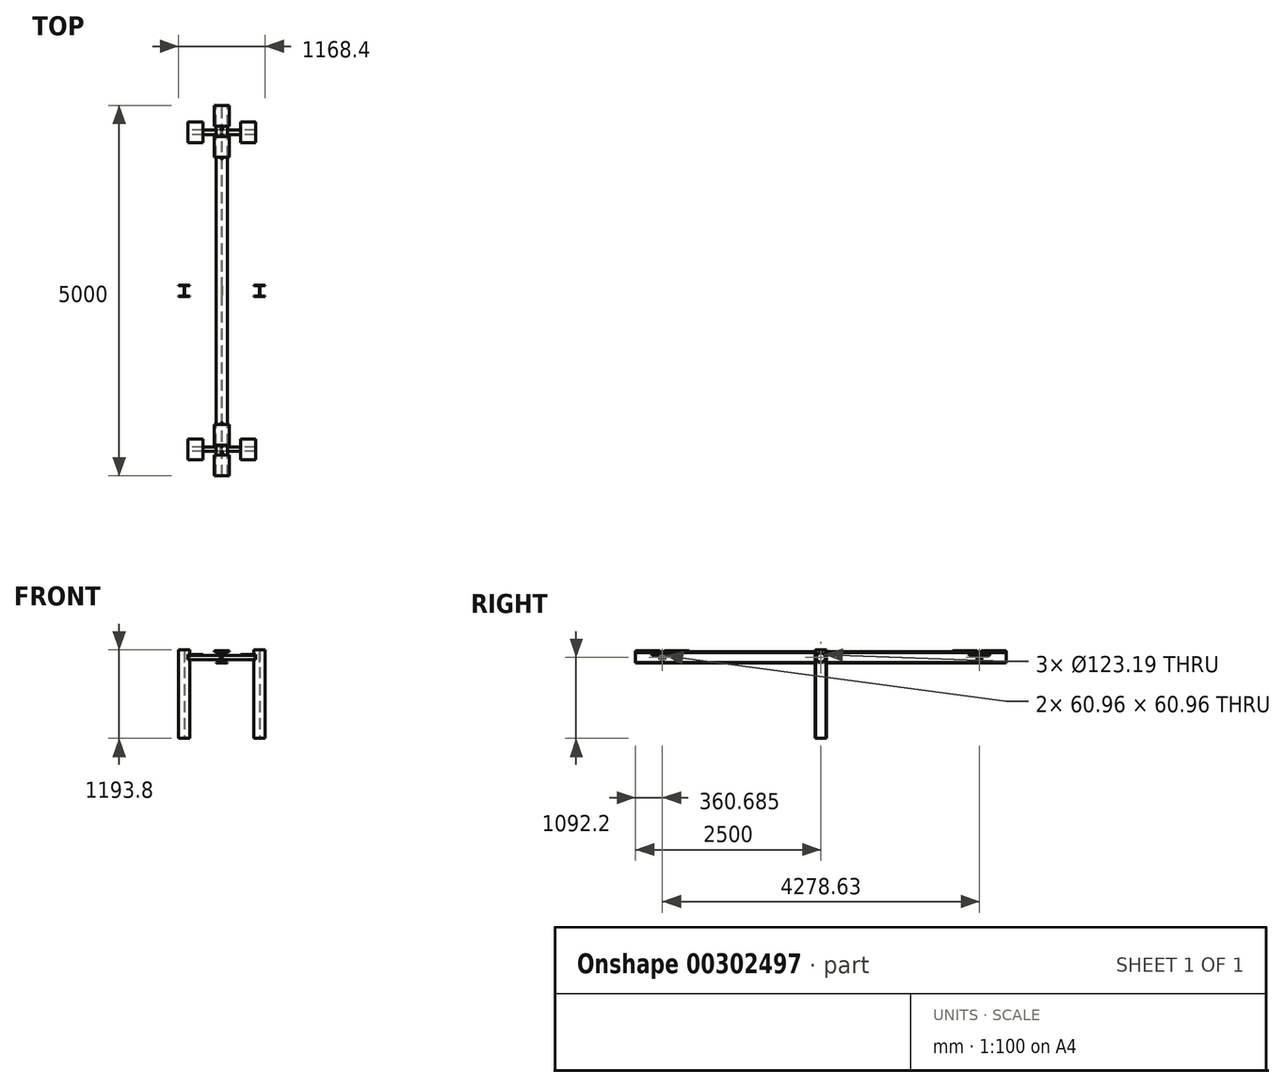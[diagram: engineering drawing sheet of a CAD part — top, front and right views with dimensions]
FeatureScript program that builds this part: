
annotation { "Feature Type Name" : "Feature", "Feature Type Description" : "" }
export const myFeature = defineFeature(function(context is Context, id is Id, definition is map)
    precondition{}
    {
        {
            var Q0;
            Q0=qCreatedBy(makeId("Right.planeOp"),FACE);
            var sketch = newSketch(context, id + "F0", { "sketchPlane" : qUnion([Q0])});
            skCircle(sketch, "E0", {"center": v(0, 0) * mm, "radius": 60.96 * mm});
            skSolve(sketch);
        }
        {
            var Q0;
            Q0 = qSketchRegion(id + "F0", true);
            extrude(context, id + "F1", {"entities" : qUnion([Q0]), "endBound" : BoundingType.SYMMETRIC, "depth" : 1092.2 * mm});
        }
        {
            var Q0;
            Q0=qCreatedBy(makeId("Front.planeOp"),FACE);
            var sketch = newSketch(context, id + "F2", { "sketchPlane" : qUnion([Q0])});
            skLineSegment(sketch, "E1.bottom", {"start": v(-76.2, 76.2) * mm, "end": v(76.2, 76.2) * mm});
            skLineSegment(sketch, "E1.top", {"start": v(-76.2, -76.2) * mm, "end": v(76.2, -76.2) * mm});
            skPoint(sketch, "E1.middle", {"position": v(0, 0) * mm});
            skLineSegment(sketch, "E2", {"start": v(-76.2, 76.2) * mm, "end": v(-76.2, 69.09) * mm});
            skLineSegment(sketch, "E3", {"start": v(-76.2, 69.09) * mm, "end": v(-3.05, 69.09) * mm});
            skLineSegment(sketch, "E4", {"start": v(-3.05, 69.09) * mm, "end": v(-3.05, -69.09) * mm});
            skLineSegment(sketch, "E5", {"start": v(-3.05, -69.09) * mm, "end": v(-76.2, -69.09) * mm});
            skLineSegment(sketch, "E6", {"start": v(-76.2, -69.09) * mm, "end": v(-76.2, -76.2) * mm});
            skLineSegment(sketch, "E7", {"start": v(76.2, -76.2) * mm, "end": v(76.2, -69.09) * mm});
            skLineSegment(sketch, "E8", {"start": v(76.2, -69.09) * mm, "end": v(3.05, -69.09) * mm});
            skLineSegment(sketch, "E9", {"start": v(3.05, -69.09) * mm, "end": v(3.05, 69.09) * mm});
            skLineSegment(sketch, "E10", {"start": v(3.05, 69.09) * mm, "end": v(76.2, 69.09) * mm});
            skLineSegment(sketch, "E11", {"start": v(76.2, 69.09) * mm, "end": v(76.2, 76.2) * mm});
            skLineSegment(sketch, "E12", {"start": v(0, 0) * mm, "end": v(507.97, -5.28) * mm, "construction": true});
            skSolve(sketch);
        }
        {
            var Q0;
            Q0 = qSketchRegion(id + "F2", true);
            extrude(context, id + "F3", {"entities" : qUnion([Q0]), "endBound" : BoundingType.SYMMETRIC, "depth" : 4999.99 * mm});
        }
        {
            var Q0;
            Q0=qCreatedBy(makeId("Top.planeOp"),FACE);
            var sketch = newSketch(context, id + "F4", { "sketchPlane" : qUnion([Q0])});
            skLineSegment(sketch, "E13", {"start": v(0, 0) * mm, "end": v(508, 0) * mm});
            skLineSegment(sketch, "E14.bottom", {"start": v(431.8, 76.2) * mm, "end": v(584.2, 76.2) * mm});
            skLineSegment(sketch, "E14.top", {"start": v(431.8, -76.2) * mm, "end": v(584.2, -76.2) * mm});
            skPoint(sketch, "E14.middle", {"position": v(508, 0) * mm});
            skLineSegment(sketch, "E15", {"start": v(431.8, 76.2) * mm, "end": v(431.8, 69.09) * mm});
            skLineSegment(sketch, "E16", {"start": v(431.8, 69.09) * mm, "end": v(504.95, 69.09) * mm});
            skLineSegment(sketch, "E17", {"start": v(504.95, 69.09) * mm, "end": v(504.95, -69.09) * mm});
            skLineSegment(sketch, "E18", {"start": v(504.95, -69.09) * mm, "end": v(431.8, -69.09) * mm});
            skLineSegment(sketch, "E19", {"start": v(431.8, -69.09) * mm, "end": v(431.8, -76.2) * mm});
            skLineSegment(sketch, "E20", {"start": v(584.2, -76.2) * mm, "end": v(584.2, -69.09) * mm});
            skLineSegment(sketch, "E21", {"start": v(584.2, -69.09) * mm, "end": v(511.05, -69.09) * mm});
            skLineSegment(sketch, "E22", {"start": v(511.05, -69.09) * mm, "end": v(511.05, 69.09) * mm});
            skLineSegment(sketch, "E23", {"start": v(511.05, 69.09) * mm, "end": v(584.2, 69.09) * mm});
            skLineSegment(sketch, "E24", {"start": v(584.2, 69.09) * mm, "end": v(584.2, 76.2) * mm});
            skLineSegment(sketch, "E25.MirrorCS", {"start": v(-431.8, 69.09) * mm, "end": v(-504.95, 69.09) * mm});
            skLineSegment(sketch, "E26.MirrorCS", {"start": v(-431.8, 76.2) * mm, "end": v(-584.2, 76.2) * mm});
            skLineSegment(sketch, "E27.MirrorCS", {"start": v(-431.8, 76.2) * mm, "end": v(-431.8, 69.09) * mm});
            skLineSegment(sketch, "E28.MirrorCS", {"start": v(-584.2, -76.2) * mm, "end": v(-584.2, -69.09) * mm});
            skLineSegment(sketch, "E29.MirrorCS", {"start": v(-431.8, -69.09) * mm, "end": v(-431.8, -76.2) * mm});
            skLineSegment(sketch, "E30.MirrorCS", {"start": v(-431.8, -76.2) * mm, "end": v(-584.2, -76.2) * mm});
            skLineSegment(sketch, "E31.MirrorCS", {"start": v(-504.95, 69.09) * mm, "end": v(-504.95, -69.09) * mm});
            skLineSegment(sketch, "E32.MirrorCS", {"start": v(-504.95, -69.09) * mm, "end": v(-431.8, -69.09) * mm});
            skPoint(sketch, "E33.MirrorP", {"position": v(-508, 0) * mm});
            skLineSegment(sketch, "E34.MirrorCS", {"start": v(-511.05, -69.09) * mm, "end": v(-511.05, 69.09) * mm});
            skLineSegment(sketch, "E35.MirrorCS", {"start": v(-584.2, -69.09) * mm, "end": v(-511.05, -69.09) * mm});
            skLineSegment(sketch, "E36.MirrorCS", {"start": v(-511.05, 69.09) * mm, "end": v(-584.2, 69.09) * mm});
            skLineSegment(sketch, "E37.MirrorCS", {"start": v(0, 0) * mm, "end": v(-508, 0) * mm});
            skLineSegment(sketch, "E38.MirrorCS", {"start": v(-584.2, 69.09) * mm, "end": v(-584.2, 76.2) * mm});
            skSolve(sketch);
        }
        {
            var Q0;
            Q0 = qSketchRegion(id + "F4", true);
            extrude(context, id + "F5", {"entities" : qUnion([Q0]), "oppositeDirection" : true, "depth" : 1092.2 * mm});
        }
        {
            var Q0;
            Q0=makeQuery(id+"F5.opExtrude","CAP_FACE",FACE,{"disambiguationData":[OSD([sQuery(id+"F4.wireOp",EDGE,"E27.MirrorCS"),sQuery(id+"F4.wireOp",EDGE,"E29.MirrorCS"),sQuery(id+"F4.wireOp",EDGE,"E38.MirrorCS"),sQuery(id+"F4.wireOp",EDGE,"E28.MirrorCS"),sQuery(id+"F4.wireOp",EDGE,"E26.MirrorCS"),sQuery(id+"F4.wireOp",EDGE,"E30.MirrorCS"),sQuery(id+"F4.wireOp",EDGE,"E25.MirrorCS"),sQuery(id+"F4.wireOp",EDGE,"E31.MirrorCS"),sQuery(id+"F4.wireOp",EDGE,"E36.MirrorCS"),sQuery(id+"F4.wireOp",EDGE,"E35.MirrorCS"),sQuery(id+"F4.wireOp",EDGE,"E32.MirrorCS"),sQuery(id+"F4.wireOp",EDGE,"E34.MirrorCS")])],"isStart":true});
            var Q1;
            Q1=makeQuery(id+"F5.opExtrude","CAP_FACE",FACE,{"disambiguationData":[OSD([sQuery(id+"F4.wireOp",EDGE,"E14.bottom"),sQuery(id+"F4.wireOp",EDGE,"E14.top"),sQuery(id+"F4.wireOp",EDGE,"E15"),sQuery(id+"F4.wireOp",EDGE,"E16"),sQuery(id+"F4.wireOp",EDGE,"E17"),sQuery(id+"F4.wireOp",EDGE,"E18"),sQuery(id+"F4.wireOp",EDGE,"E19"),sQuery(id+"F4.wireOp",EDGE,"E20"),sQuery(id+"F4.wireOp",EDGE,"E21"),sQuery(id+"F4.wireOp",EDGE,"E22"),sQuery(id+"F4.wireOp",EDGE,"E23"),sQuery(id+"F4.wireOp",EDGE,"E24")])],"isStart":true});
            extrude(context, id + "F6", {"entities" : qUnion([Q0, Q1]), "depth" : 101.6 * mm});
        }
        {
            var Q0;
            Q0=makeQuery(id+"F6.opExtrude","SWEPT_BODY",BODY,{"disambiguationData":[OSD([sQuery(id+"F4.wireOp",EDGE,"E27.MirrorCS"),sQuery(id+"F4.wireOp",EDGE,"E29.MirrorCS"),sQuery(id+"F4.wireOp",EDGE,"E38.MirrorCS"),sQuery(id+"F4.wireOp",EDGE,"E28.MirrorCS"),sQuery(id+"F4.wireOp",EDGE,"E26.MirrorCS"),sQuery(id+"F4.wireOp",EDGE,"E30.MirrorCS"),sQuery(id+"F4.wireOp",EDGE,"E25.MirrorCS"),sQuery(id+"F4.wireOp",EDGE,"E31.MirrorCS"),sQuery(id+"F4.wireOp",EDGE,"E36.MirrorCS"),sQuery(id+"F4.wireOp",EDGE,"E35.MirrorCS"),sQuery(id+"F4.wireOp",EDGE,"E32.MirrorCS"),sQuery(id+"F4.wireOp",EDGE,"E34.MirrorCS")])]});
            var Q1;
            Q1=makeQuery(id+"F5.opExtrude","SWEPT_BODY",BODY,{"disambiguationData":[OSD([sQuery(id+"F4.wireOp",EDGE,"E27.MirrorCS"),sQuery(id+"F4.wireOp",EDGE,"E29.MirrorCS"),sQuery(id+"F4.wireOp",EDGE,"E38.MirrorCS"),sQuery(id+"F4.wireOp",EDGE,"E28.MirrorCS"),sQuery(id+"F4.wireOp",EDGE,"E26.MirrorCS"),sQuery(id+"F4.wireOp",EDGE,"E30.MirrorCS"),sQuery(id+"F4.wireOp",EDGE,"E25.MirrorCS"),sQuery(id+"F4.wireOp",EDGE,"E31.MirrorCS"),sQuery(id+"F4.wireOp",EDGE,"E36.MirrorCS"),sQuery(id+"F4.wireOp",EDGE,"E35.MirrorCS"),sQuery(id+"F4.wireOp",EDGE,"E32.MirrorCS"),sQuery(id+"F4.wireOp",EDGE,"E34.MirrorCS")])]});
            booleanBodies(context, id + "F7", {"operationType" : BooleanOperationType.UNION, "tools" : qUnion([Q0, Q1])});
        }
        {
            var Q0;
            Q0=makeQuery(id+"F6.opExtrude","SWEPT_BODY",BODY,{"disambiguationData":[OSD([sQuery(id+"F4.wireOp",EDGE,"E14.bottom"),sQuery(id+"F4.wireOp",EDGE,"E14.top"),sQuery(id+"F4.wireOp",EDGE,"E15"),sQuery(id+"F4.wireOp",EDGE,"E16"),sQuery(id+"F4.wireOp",EDGE,"E17"),sQuery(id+"F4.wireOp",EDGE,"E18"),sQuery(id+"F4.wireOp",EDGE,"E19"),sQuery(id+"F4.wireOp",EDGE,"E20"),sQuery(id+"F4.wireOp",EDGE,"E21"),sQuery(id+"F4.wireOp",EDGE,"E22"),sQuery(id+"F4.wireOp",EDGE,"E23"),sQuery(id+"F4.wireOp",EDGE,"E24")])]});
            var Q1;
            Q1=makeQuery(id+"F5.opExtrude","SWEPT_BODY",BODY,{"disambiguationData":[OSD([sQuery(id+"F4.wireOp",EDGE,"E14.bottom"),sQuery(id+"F4.wireOp",EDGE,"E14.top"),sQuery(id+"F4.wireOp",EDGE,"E15"),sQuery(id+"F4.wireOp",EDGE,"E16"),sQuery(id+"F4.wireOp",EDGE,"E17"),sQuery(id+"F4.wireOp",EDGE,"E18"),sQuery(id+"F4.wireOp",EDGE,"E19"),sQuery(id+"F4.wireOp",EDGE,"E20"),sQuery(id+"F4.wireOp",EDGE,"E21"),sQuery(id+"F4.wireOp",EDGE,"E22"),sQuery(id+"F4.wireOp",EDGE,"E23"),sQuery(id+"F4.wireOp",EDGE,"E24")])]});
            booleanBodies(context, id + "F8", {"operationType" : BooleanOperationType.UNION, "tools" : qUnion([Q0, Q1])});
        }
        {
            var Q0;
            Q0=makeQuery(id+"F3.opExtrude","SWEPT_FACE",FACE,{"disambiguationData":[OSD([sQuery(id+"F2.wireOp",EDGE,"E9")])]});
            var sketch = newSketch(context, id + "F9", { "sketchPlane" : qUnion([Q0])});
            skCircle(sketch, "E39", {"center": v(0, 0) * mm, "radius": 61.6 * mm});
            skSolve(sketch);
        }
        {
            var Q0;
            Q0 = qSketchRegion(id + "F9", true);
            extrude(context, id + "F10", {"entities" : qUnion([Q0]), "operationType" : NewBodyOperationType.REMOVE, "endBound" : BoundingType.THROUGH_ALL, "oppositeDirection" : true, "depth" : 25.4 * mm});
        }
        {
            var Q0;
            {var subQ0=sQuery(id+"F4.wireOp",EDGE,"E22");Q0=makeQuery(id+"F8.opBoolean","MERGE",FACE,{"derivedFrom":[makeQuery(id+"F5.opExtrude","SWEPT_FACE",FACE,{"disambiguationData":[OSD([subQ0])]}),makeQuery(id+"F6.opExtrude","SWEPT_FACE",FACE,{"disambiguationData":[OSD([subQ0])]})]});}
            var sketch = newSketch(context, id + "F11", { "sketchPlane" : qUnion([Q0])});
            skCircle(sketch, "E40", {"center": v(0, 0) * mm, "radius": 61.6 * mm});
            skSolve(sketch);
        }
        {
            var Q0;
            Q0 = qSketchRegion(id + "F11", true);
            extrude(context, id + "F12", {"entities" : qUnion([Q0]), "operationType" : NewBodyOperationType.REMOVE, "endBound" : BoundingType.THROUGH_ALL, "oppositeDirection" : true, "depth" : 25.4 * mm});
        }
        {
            var Q0;
            {var subQ0=sQuery(id+"F4.wireOp",EDGE,"E34.MirrorCS");Q0=makeQuery(id+"F7.opBoolean","MERGE",FACE,{"derivedFrom":[makeQuery(id+"F5.opExtrude","SWEPT_FACE",FACE,{"disambiguationData":[OSD([subQ0])]}),makeQuery(id+"F6.opExtrude","SWEPT_FACE",FACE,{"disambiguationData":[OSD([subQ0])]})]});}
            var sketch = newSketch(context, id + "F13", { "sketchPlane" : qUnion([Q0])});
            skCircle(sketch, "E41", {"center": v(0, 0) * mm, "radius": 61.6 * mm});
            skSolve(sketch);
        }
        {
            var Q0;
            Q0 = qSketchRegion(id + "F13", true);
            extrude(context, id + "F14", {"entities" : qUnion([Q0]), "operationType" : NewBodyOperationType.REMOVE, "endBound" : BoundingType.THROUGH_ALL, "oppositeDirection" : true, "depth" : 25.4 * mm});
        }
        {
            var Q0;
            Q0=makeQuery(id+"F3.opExtrude","SWEPT_FACE",FACE,{"disambiguationData":[OSD([sQuery(id+"F2.wireOp",EDGE,"E1.bottom")])]});
            var sketch = newSketch(context, id + "F15", { "sketchPlane" : qUnion([Q0])});
            skLineSegment(sketch, "E42", {"start": v(0, 0) * mm, "end": v(0, -2360.3) * mm});
            skLineSegment(sketch, "E43.bottom", {"start": v(-101.6, -2220.6) * mm, "end": v(101.6, -2220.6) * mm});
            skLineSegment(sketch, "E43.top", {"start": v(-101.6, -2500) * mm, "end": v(101.6, -2500) * mm});
            skLineSegment(sketch, "E43.left", {"start": v(-101.6, -2220.6) * mm, "end": v(-101.6, -2500) * mm});
            skLineSegment(sketch, "E43.right", {"start": v(101.6, -2220.6) * mm, "end": v(101.6, -2500) * mm});
            skPoint(sketch, "E43.middle", {"position": v(0, -2360.3) * mm});
            skLineSegment(sketch, "E44.bottom", {"start": v(-101.6, -1804.04) * mm, "end": v(101.6, -1804.04) * mm});
            skLineSegment(sketch, "E44.top", {"start": v(-101.6, -2083.43) * mm, "end": v(101.6, -2083.43) * mm});
            skLineSegment(sketch, "E44.left", {"start": v(-101.6, -1804.04) * mm, "end": v(-101.6, -2083.43) * mm});
            skLineSegment(sketch, "E44.right", {"start": v(101.6, -1804.04) * mm, "end": v(101.6, -2083.43) * mm});
            skPoint(sketch, "E44.middle", {"position": v(0, -1943.74) * mm});
            skCircle(sketch, "E45", {"center": v(0, -2207.9) * mm, "radius": 12.7 * mm});
            skCircle(sketch, "E46", {"center": v(0, -2182.5) * mm, "radius": 12.7 * mm});
            skCircle(sketch, "E47", {"center": v(0, -1791.34) * mm, "radius": 12.7 * mm});
            skCircle(sketch, "E48", {"center": v(0, -2096.14) * mm, "radius": 12.7 * mm});
            skCircle(sketch, "E49.MirrorC", {"center": v(0, 2182.5) * mm, "radius": 12.7 * mm});
            skLineSegment(sketch, "E50.MirrorCS", {"start": v(101.6, 1804.04) * mm, "end": v(101.6, 2083.43) * mm});
            skLineSegment(sketch, "E51.MirrorCS", {"start": v(-101.6, 2220.6) * mm, "end": v(101.6, 2220.6) * mm});
            skLineSegment(sketch, "E52.MirrorCS", {"start": v(-101.6, 2083.43) * mm, "end": v(101.6, 2083.43) * mm});
            skPoint(sketch, "E53.MirrorP", {"position": v(0, 1943.74) * mm});
            skLineSegment(sketch, "E54.MirrorCS", {"start": v(101.6, 2220.6) * mm, "end": v(101.6, 2500) * mm});
            skLineSegment(sketch, "E55.MirrorCS", {"start": v(-101.6, 1804.04) * mm, "end": v(101.6, 1804.04) * mm});
            skCircle(sketch, "E56.MirrorC", {"center": v(0, 2207.9) * mm, "radius": 12.7 * mm});
            skCircle(sketch, "E57.MirrorC", {"center": v(0, 1791.34) * mm, "radius": 12.7 * mm});
            skLineSegment(sketch, "E58.MirrorCS", {"start": v(0, 0) * mm, "end": v(0, 2360.3) * mm});
            skLineSegment(sketch, "E59.MirrorCS", {"start": v(-101.6, 1804.04) * mm, "end": v(-101.6, 2083.43) * mm});
            skCircle(sketch, "E60.MirrorC", {"center": v(0, 2096.14) * mm, "radius": 12.7 * mm});
            skLineSegment(sketch, "E61.MirrorCS", {"start": v(-101.6, 2500) * mm, "end": v(101.6, 2500) * mm});
            skLineSegment(sketch, "E62.MirrorCS", {"start": v(-101.6, 2220.6) * mm, "end": v(-101.6, 2500) * mm});
            skPoint(sketch, "E63.MirrorP", {"position": v(0, 2360.3) * mm});
            skSolve(sketch);
        }
        {
            var Q0;
            Q0 = qSketchRegion(id + "F15", true);
            extrude(context, id + "F16", {"entities" : qUnion([Q0]), "depth" : 12.7 * mm});
        }
        {
            var Q0;
            Q0=qCreatedBy(makeId("Right.planeOp"),FACE);
            var sketch = newSketch(context, id + "F17", { "sketchPlane" : qUnion([Q0])});
            skLineSegment(sketch, "E64", {"start": v(0, 0) * mm, "end": v(-2139.32, 0) * mm});
            skLineSegment(sketch, "E65.bottom", {"start": v(-2169.8, 30.48) * mm, "end": v(-2108.83, 30.48) * mm});
            skLineSegment(sketch, "E65.top", {"start": v(-2169.8, -30.48) * mm, "end": v(-2108.83, -30.48) * mm});
            skLineSegment(sketch, "E65.left", {"start": v(-2169.8, 30.48) * mm, "end": v(-2169.8, -30.48) * mm});
            skLineSegment(sketch, "E65.right", {"start": v(-2108.83, 30.48) * mm, "end": v(-2108.83, -30.48) * mm});
            skPoint(sketch, "E65.middle", {"position": v(-2139.32, 0) * mm});
            skPoint(sketch, "E66.MirrorP", {"position": v(2139.32, 0) * mm});
            skLineSegment(sketch, "E67.MirrorCS", {"start": v(2169.8, -30.48) * mm, "end": v(2108.83, -30.48) * mm});
            skLineSegment(sketch, "E68.MirrorCS", {"start": v(2108.83, 30.48) * mm, "end": v(2108.83, -30.48) * mm});
            skLineSegment(sketch, "E69.MirrorCS", {"start": v(2169.8, 30.48) * mm, "end": v(2108.83, 30.48) * mm});
            skLineSegment(sketch, "E70.MirrorCS", {"start": v(2169.8, 30.48) * mm, "end": v(2169.8, -30.48) * mm});
            skSolve(sketch);
        }
        {
            var Q0;
            Q0 = qSketchRegion(id + "F17", true);
            extrude(context, id + "F18", {"entities" : qUnion([Q0]), "endBound" : BoundingType.SYMMETRIC, "depth" : 914.4 * mm});
        }
        {
            var Q0;
            Q0=makeQuery(id+"F18.opExtrude","SWEPT_FACE",FACE,{"disambiguationData":[OSD([sQuery(id+"F17.wireOp",EDGE,"E65.bottom")])]});
            var sketch = newSketch(context, id + "F19", { "sketchPlane" : qUnion([Q0])});
            skLineSegment(sketch, "E71", {"start": v(457.2, -2139.32) * mm, "end": v(355.6, -2139.32) * mm});
            skLineSegment(sketch, "E72.bottom", {"start": v(254, -1999.61) * mm, "end": v(457.2, -1999.61) * mm});
            skLineSegment(sketch, "E72.top", {"start": v(254, -2279.01) * mm, "end": v(457.2, -2279.01) * mm});
            skLineSegment(sketch, "E72.left", {"start": v(254, -1999.61) * mm, "end": v(254, -2279.01) * mm});
            skLineSegment(sketch, "E72.right", {"start": v(457.2, -1999.61) * mm, "end": v(457.2, -2279.01) * mm});
            skPoint(sketch, "E72.middle", {"position": v(355.6, -2139.32) * mm});
            skLineSegment(sketch, "E73.MirrorCS", {"start": v(-457.2, -2139.32) * mm, "end": v(-355.6, -2139.32) * mm});
            skLineSegment(sketch, "E74.MirrorCS", {"start": v(-457.2, -1999.61) * mm, "end": v(-457.2, -2279.01) * mm});
            skLineSegment(sketch, "E75.MirrorCS", {"start": v(-254, -1999.61) * mm, "end": v(-254, -2279.01) * mm});
            skLineSegment(sketch, "E76.MirrorCS", {"start": v(-254, -2279.01) * mm, "end": v(-457.2, -2279.01) * mm});
            skLineSegment(sketch, "E77.MirrorCS", {"start": v(-254, -1999.61) * mm, "end": v(-457.2, -1999.61) * mm});
            skPoint(sketch, "E78.MirrorP", {"position": v(-355.6, -2139.32) * mm});
            skLineSegment(sketch, "E79.MirrorCS", {"start": v(457.2, 2139.32) * mm, "end": v(355.6, 2139.32) * mm});
            skLineSegment(sketch, "E80.MirrorCS", {"start": v(457.2, 1999.61) * mm, "end": v(457.2, 2279.01) * mm});
            skPoint(sketch, "E81.MirrorP", {"position": v(355.6, 2139.32) * mm});
            skLineSegment(sketch, "E82.MirrorCS", {"start": v(254, 1999.61) * mm, "end": v(254, 2279.01) * mm});
            skLineSegment(sketch, "E83.MirrorCS", {"start": v(254, 2279.01) * mm, "end": v(457.2, 2279.01) * mm});
            skLineSegment(sketch, "E84.MirrorCS", {"start": v(254, 1999.61) * mm, "end": v(457.2, 1999.61) * mm});
            skLineSegment(sketch, "E85.MirrorCS", {"start": v(-457.2, 2139.32) * mm, "end": v(-355.6, 2139.32) * mm});
            skLineSegment(sketch, "E86.MirrorCS", {"start": v(-457.2, 1999.61) * mm, "end": v(-457.2, 2279.01) * mm});
            skPoint(sketch, "E87.MirrorP", {"position": v(-355.6, 2139.32) * mm});
            skLineSegment(sketch, "E88.MirrorCS", {"start": v(-254, 1999.61) * mm, "end": v(-254, 2279.01) * mm});
            skLineSegment(sketch, "E89.MirrorCS", {"start": v(-254, 2279.01) * mm, "end": v(-457.2, 2279.01) * mm});
            skLineSegment(sketch, "E90.MirrorCS", {"start": v(-254, 1999.61) * mm, "end": v(-457.2, 1999.61) * mm});
            skSolve(sketch);
        }
        {
            var Q0;
            Q0 = qSketchRegion(id + "F19", true);
            extrude(context, id + "F20", {"entities" : qUnion([Q0]), "operationType" : NewBodyOperationType.ADD, "depth" : 12.7 * mm});
        }
        {
            var Q0;
            Q0=makeQuery(id+"F3.opExtrude","SWEPT_FACE",FACE,{"disambiguationData":[OSD([sQuery(id+"F2.wireOp",EDGE,"E9")])]});
            var sketch = newSketch(context, id + "F21", { "sketchPlane" : qUnion([Q0])});
            skLineSegment(sketch, "E91", {"start": v(0, 0) * mm, "end": v(-2139.32, 0) * mm});
            skLineSegment(sketch, "E92.bottom", {"start": v(-2169.8, 30.48) * mm, "end": v(-2108.83, 30.48) * mm});
            skLineSegment(sketch, "E92.top", {"start": v(-2169.8, -30.48) * mm, "end": v(-2108.83, -30.48) * mm});
            skLineSegment(sketch, "E92.left", {"start": v(-2169.8, 30.48) * mm, "end": v(-2169.8, -30.48) * mm});
            skLineSegment(sketch, "E92.right", {"start": v(-2108.83, 30.48) * mm, "end": v(-2108.83, -30.48) * mm});
            skPoint(sketch, "E92.middle", {"position": v(-2139.32, 0) * mm});
            skLineSegment(sketch, "E93.MirrorCS", {"start": v(2108.83, 30.48) * mm, "end": v(2108.83, -30.48) * mm});
            skLineSegment(sketch, "E94.MirrorCS", {"start": v(2169.8, 30.48) * mm, "end": v(2169.8, -30.48) * mm});
            skLineSegment(sketch, "E95.MirrorCS", {"start": v(2169.8, -30.48) * mm, "end": v(2108.83, -30.48) * mm});
            skLineSegment(sketch, "E96.MirrorCS", {"start": v(2169.8, 30.48) * mm, "end": v(2108.83, 30.48) * mm});
            skLineSegment(sketch, "E97.MirrorCS", {"start": v(0, 0) * mm, "end": v(2139.32, 0) * mm});
            skPoint(sketch, "E98.MirrorP", {"position": v(2139.32, 0) * mm});
            skSolve(sketch);
        }
        {
            var Q0;
            Q0 = qSketchRegion(id + "F21", true);
            extrude(context, id + "F22", {"entities" : qUnion([Q0]), "operationType" : NewBodyOperationType.REMOVE, "oppositeDirection" : true, "depth" : 25.4 * mm});
        }
    });
